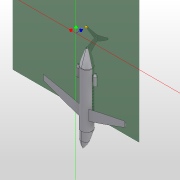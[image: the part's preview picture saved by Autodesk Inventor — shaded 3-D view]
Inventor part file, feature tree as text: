
AUTODESK INVENTOR PART (.ipt)
format: ipt  version: 2016 (Build 200138000, 138)  size: 953,344 bytes
history: native  units: mm
features: sketch x20, plane x12, extrude x7, other x6, loft x5, fillet x4, mirror x4, projected_geometry x2
ambient origin geometry x8: Origin, YZ Plane, XZ Plane, XY Plane, X Axis, Y Axis, Z Axis, Center Point
bodies: Solid1 (feature_tree)
feature tree (60):
  other  "Landing Surface"
  extrude  "Extrusion1"  Depth=200.0mm
  plane  "Work Plane4"
  sketch  "Sketch5"  dims[d17=80.0mm d18=20.0mm]
  plane  "Work Plane5"
  loft  "Loft1"
  plane  "Work Plane6"
  sketch  "Sketch7"  dims[d22=20.0mm d23=0.0mm d24=90.0deg d25=0.0mm d26=90.0deg]
  plane  "Work Plane7"
  sketch  "Sketch8"  dims[d27=0.0mm d28=90.0deg d29=80.0mm]
  other  "Work Point6"
  loft  "Loft2"
  fillet  "Fillet1"  Radius=80.0mm
  plane  "Work Plane8"
  sketch  "Sketch9"  dims[d30=50.0mm d35=20.0mm]
  plane  "Work Plane9"
  sketch  "Sketch10"  dims[d36=30.0mm d37=40.0mm d38=10.0mm]
  plane  "Work Plane10"
  loft  "Loft3"
  fillet  "Fillet2"  [1 undecoded]
  sketch  "Sketch12"  dims[d43=0.0mm d44=90.0deg d45=50.0mm]
  plane  "Work Plane11"
  sketch  "Sketch13"  dims[d46=100.0mm d47=70.0mm d48=70.0mm]
  plane  "Work Plane12"
  loft  "Loft4"
  mirror  "Mirror1"
  extrude  "Extrusion4"  Depth=20.0mm
  sketch  "Sketch16"  dims[d54=50.0mm]
  plane  "Work Plane13"
  sketch  "Sketch17"  dims[d55=50.0mm]
  plane  "Work Plane14"
  loft  "Loft5"
  mirror  "Mirror2"
  fillet  "Fillet3"  Radius=10.0mm
  extrude  "Extrusion5"  TaperAngle=0.0deg  [1 undecoded]
  extrude  "Extrusion6"  Depth=50.0mm
  extrude  "Extrusion7"  Depth=100.0mm
  mirror  "Mirror3"
  fillet  "Fillet4"  Radius=70.0mm
  plane  "Work Plane15"
  extrude  "Extrusion8"  Depth=50.0mm
  extrude  "Extrusion9"  Depth=80.0mm
  mirror  "Mirror4"
  other  "Insertion Point1"
  sketch  "Sketch1"  dims[d6=1000.0mm d7=0.0mm d8=200.0mm]
  projected_geometry  "Projected Loop1"
  sketch  "Sketch6"  dims[d19=90.0mm d20=80.0mm d21=80.0mm]
  other  "Edges1"
  other  "Edges2"
  sketch  "Sketch11"  dims[d39=0.0mm d40=90.0deg d41=0.0mm d42=90.0deg]
  other  "Edges3"
  sketch  "Sketch14"  dims[d49=60.0mm d51=50.0mm]
  sketch  "Sketch15"  dims[d52=35.0mm d53=80.0mm]
  sketch  "Sketch18"  dims[d56=35.0mm]
  sketch  "Sketch19"  dims[d57=30.0mm]
  sketch  "Sketch20"  dims[d58=40.0mm]
  sketch  "Sketch21"  dims[d59=30.0mm]
  projected_geometry  "Projected Loop2"
  sketch  "Sketch22"  dims[d60=100.0mm]
  sketch  "Sketch23"  dims[d61=25.0mm d62=15.0mm d63=20.0mm d64=30.0mm d65=10.0mm d67=40.0mm d68=0.0mm d69=90.0deg d70=0.0mm d71=90.0deg d72=0.0mm d73=90.0deg d74=0.0mm d75=90.0deg d76=50.0mm d77=200.0mm d78=50.0mm d79=35.0mm d80=20.0mm d83=450.0mm d85=30.0mm d86=15.0mm d89=300.0mm d90=100.0mm d91=20.0mm d94=10.0mm d96=20.0mm d97=120.0mm d98=150.0mm d99=0.0mm d100=90.0deg d101=0.0mm d102=90.0deg d103=0.0mm d104=90.0deg d105=150.0mm d106=150.0mm d107=60.0mm d119=100.0mm d120=150.0mm d121=170.0mm d122=20.0mm d123=0.0mm d124=20.0mm d125=15.0mm d126=100.0mm d127=70.0mm d128=50.0mm d129=15.0mm d130=10.0mm d131=100.0mm d132=30.0mm d133=70.0mm d134=5.0mm d135=5.0mm d136=0.0mm d137=90.0deg d138=0.0mm d139=90.0deg d140=0.0mm d141=90.0deg d142=9.0mm d143=100.0mm d144=900.0mm d145=10.0mm d146=250.0mm d147=0.0mm d148=60.0mm d149=150.0mm d150=0.0mm d151=50.0mm d152=-3.490659mm d153=5.0mm d154=-90.0mm d155=2.0mm d156=100.0mm d157=0.0mm d158=80.0mm d160=50.0mm d161=10.0mm d163=10.0mm d165=100.0mm d166=0.0mm d180=40.0mm d182=50.0mm d183=10.0mm d185=10.0mm]
note: 2 required parameter values undecoded (feature->parameter linkage not recoverable at this tier; creation-order binding heuristic only, values carry confidence <= 0.55)
